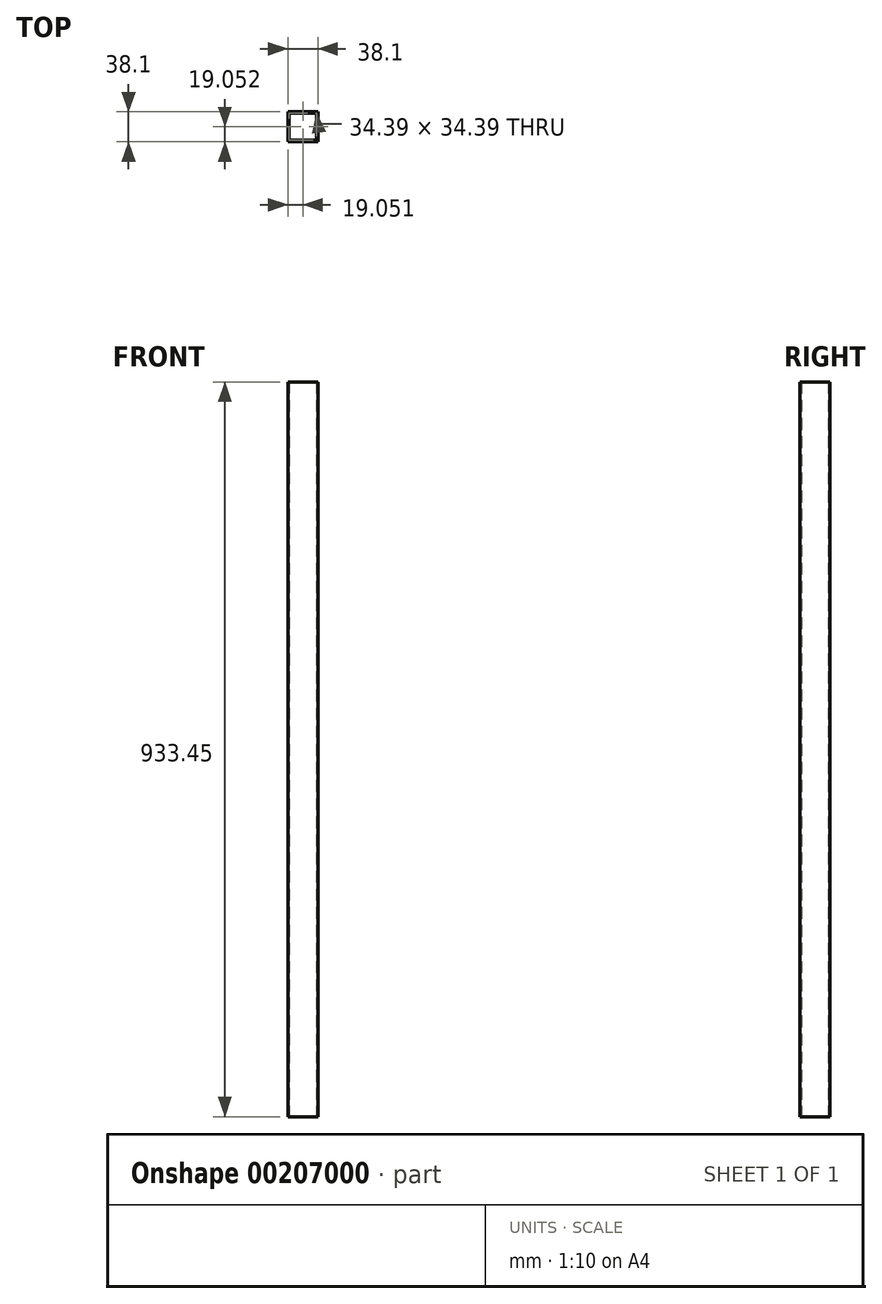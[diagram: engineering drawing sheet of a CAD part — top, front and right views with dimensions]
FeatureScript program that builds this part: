
annotation { "Feature Type Name" : "Feature", "Feature Type Description" : "" }
export const myFeature = defineFeature(function(context is Context, id is Id, definition is map)
    precondition{}
    {
        {
            var Q0;
            Q0=qCreatedBy(makeId("Top.planeOp"),FACE);
            var sketch = newSketch(context, id + "F0", { "sketchPlane" : qUnion([Q0])});
            skLineSegment(sketch, "E0.bottom", {"start": v(-20.4, -12.46) * mm, "end": v(17.7, -12.46) * mm});
            skLineSegment(sketch, "E0.top", {"start": v(-20.4, 25.64) * mm, "end": v(17.7, 25.64) * mm});
            skLineSegment(sketch, "E0.left", {"start": v(-20.4, -12.46) * mm, "end": v(-20.4, 25.64) * mm});
            skLineSegment(sketch, "E0.right", {"start": v(17.7, -12.46) * mm, "end": v(17.7, 25.64) * mm});
            skLineSegment(sketch, "E1.bottom", {"start": v(-18.54, -10.6) * mm, "end": v(15.85, -10.6) * mm});
            skLineSegment(sketch, "E1.top", {"start": v(-18.54, 23.79) * mm, "end": v(15.85, 23.79) * mm});
            skLineSegment(sketch, "E1.left", {"start": v(-18.54, -10.6) * mm, "end": v(-18.54, 23.79) * mm});
            skLineSegment(sketch, "E1.right", {"start": v(15.85, -10.6) * mm, "end": v(15.85, 23.79) * mm});
            skSolve(sketch);
        }
        {
            var Q0;
            Q0=makeQuery(id+"F0.imprint","IMPRINT",FACE,{"disambiguationData":[TD([[makeQuery(id+"F0.imprint","IMPRINT",EDGE,{"derivedFrom":sQuery(id+"F0.wireOp",EDGE,"E0.bottom")}),1.0]])]});
            extrude(context, id + "F1", {"entities" : qUnion([Q0]), "depth" : 933.45 * mm});
        }
    });
